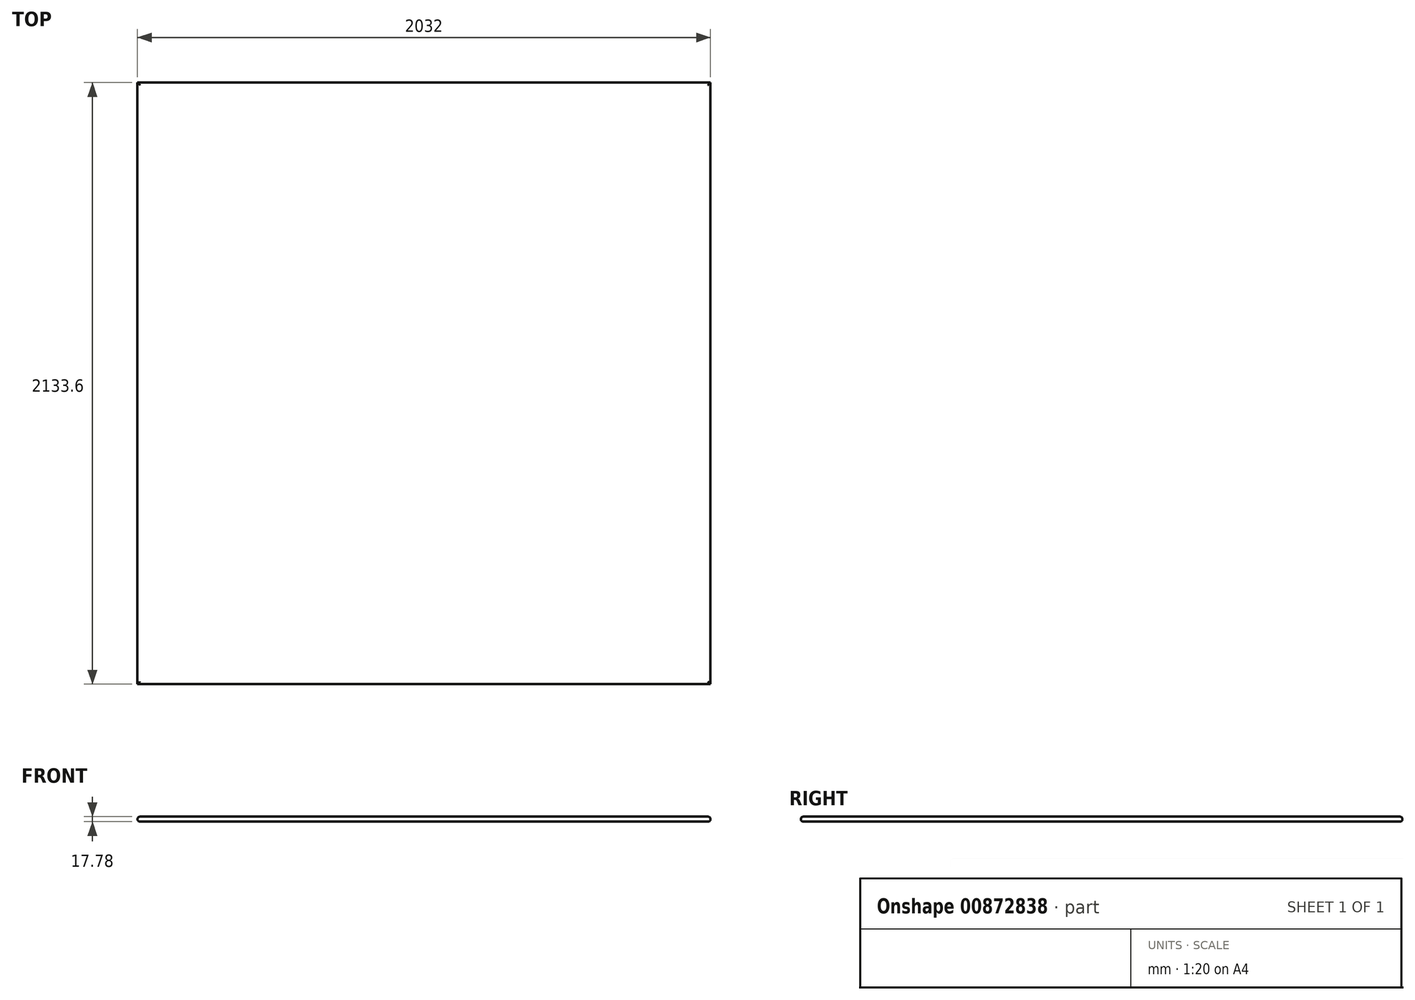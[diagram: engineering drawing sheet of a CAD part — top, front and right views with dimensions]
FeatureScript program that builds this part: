
annotation { "Feature Type Name" : "Feature", "Feature Type Description" : "" }
export const myFeature = defineFeature(function(context is Context, id is Id, definition is map)
    precondition{}
    {
        {
            var Q0;
            Q0=qCreatedBy(makeId("Top.planeOp"),FACE);
            var sketch = newSketch(context, id + "F0", { "sketchPlane" : qUnion([Q0])});
            skLineSegment(sketch, "E0.bottom", {"start": v(1016, -1066.8) * mm, "end": v(-1016, -1066.8) * mm});
            skLineSegment(sketch, "E0.top", {"start": v(1016, 1066.8) * mm, "end": v(-1016, 1066.8) * mm});
            skLineSegment(sketch, "E0.left", {"start": v(1016, -1066.8) * mm, "end": v(1016, 1066.8) * mm});
            skLineSegment(sketch, "E0.right", {"start": v(-1016, -1066.8) * mm, "end": v(-1016, 1066.8) * mm});
            skPoint(sketch, "E0.middle", {"position": v(0, 0) * mm});
            skSolve(sketch);
        }
        {
            var Q0;
            Q0=makeQuery(id+"F0.imprint","IMPRINT",FACE,{"disambiguationData":[TD([[makeQuery(id+"F0.imprint","IMPRINT",EDGE,{"derivedFrom":sQuery(id+"F0.wireOp",EDGE,"E0.bottom")}),-1.0]])]});
            extrude(context, id + "F1", {"entities" : qUnion([Q0]), "oppositeDirection" : true, "depth" : 17.78 * mm, "offsetDistance" : 25.4 * mm});
        }
        {
            var Q0;
            Q0=makeQuery(id+"F1.opExtrude","CAP_EDGE",EDGE,{"disambiguationData":[OSD([sQuery(id+"F0.wireOp",EDGE,"E0.left")])],"isStart":true});
            var Q1;
            Q1=makeQuery(id+"F1.opExtrude","CAP_EDGE",EDGE,{"disambiguationData":[OSD([sQuery(id+"F0.wireOp",EDGE,"E0.top")])],"isStart":true});
            var Q2;
            Q2=makeQuery(id+"F1.opExtrude","CAP_EDGE",EDGE,{"disambiguationData":[OSD([sQuery(id+"F0.wireOp",EDGE,"E0.right")])],"isStart":true});
            var Q3;
            Q3=makeQuery(id+"F1.opExtrude","CAP_EDGE",EDGE,{"disambiguationData":[OSD([sQuery(id+"F0.wireOp",EDGE,"E0.bottom")])],"isStart":true});
            var Q4;
            Q4=makeQuery(id+"F1.opExtrude","CAP_EDGE",EDGE,{"disambiguationData":[OSD([sQuery(id+"F0.wireOp",EDGE,"E0.bottom")])],"isStart":false});
            var Q5;
            Q5=makeQuery(id+"F1.opExtrude","CAP_EDGE",EDGE,{"disambiguationData":[OSD([sQuery(id+"F0.wireOp",EDGE,"E0.right")])],"isStart":false});
            var Q6;
            Q6=makeQuery(id+"F1.opExtrude","CAP_EDGE",EDGE,{"disambiguationData":[OSD([sQuery(id+"F0.wireOp",EDGE,"E0.top")])],"isStart":false});
            var Q7;
            Q7=makeQuery(id+"F1.opExtrude","CAP_FACE",FACE,{"disambiguationData":[OSD([sQuery(id+"F0.wireOp",EDGE,"E0.bottom"),sQuery(id+"F0.wireOp",EDGE,"E0.top"),sQuery(id+"F0.wireOp",EDGE,"E0.left"),sQuery(id+"F0.wireOp",EDGE,"E0.right")])],"isStart":false});
            fillet(context, id + "F2", {"entities" : qUnion([Q0, Q1, Q2, Q3, Q4, Q5, Q6, Q7]), "radius" : 8.9 * mm, "tangentPropagation" : true, "allowEdgeOverflow" : false});
        }
    });
